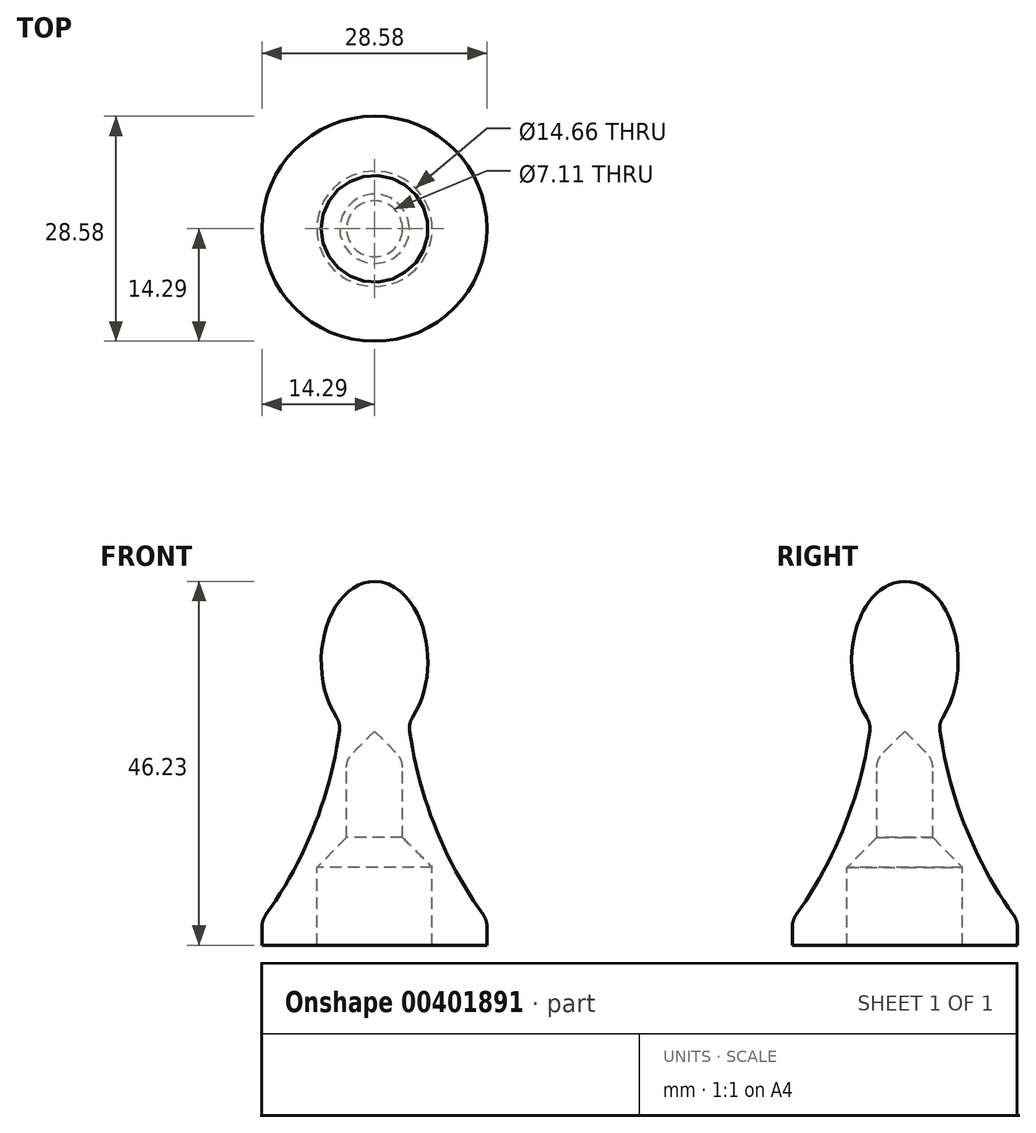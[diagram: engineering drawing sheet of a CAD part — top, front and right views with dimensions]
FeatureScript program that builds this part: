
annotation { "Feature Type Name" : "Feature", "Feature Type Description" : "" }
export const myFeature = defineFeature(function(context is Context, id is Id, definition is map)
    precondition{}
    {
        {
            var Q0;
            Q0=qCreatedBy(makeId("Front.planeOp"),FACE);
            var sketch = newSketch(context, id + "F0", { "sketchPlane" : qUnion([Q0])});
            skArc(sketch, "E0", {"start": v(-14.29, 3.18) * mm, "mid": v(-7.69, 15.07) * mm, "end": v(-4.32, 28.24) * mm});
            skLineSegment(sketch, "E1", {"start": v(-14.29, 3.17) * mm, "end": v(-14.29, 0) * mm});
            skLineSegment(sketch, "E2", {"start": v(-14.29, 0) * mm, "end": v(-7.33, 0) * mm});
            skLineSegment(sketch, "E3", {"start": v(0, 46.23) * mm, "end": v(0, 27.18) * mm});
            skLineSegment(sketch, "E4", {"start": v(-4.32, 28.24) * mm, "end": v(-1.02, 55.08) * mm, "construction": true});
            skEllipticalArc(sketch, "E5", {});
            skLineSegment(sketch, "E6", {"start": v(0, 27.18) * mm, "end": v(-2.81, 24.37) * mm});
            skLineSegment(sketch, "E7", {"start": v(-3.56, 22.57) * mm, "end": v(-3.56, 13.68) * mm});
            skLineSegment(sketch, "E8", {"start": v(-3.56, 13.68) * mm, "end": v(-7.33, 9.9) * mm});
            skLineSegment(sketch, "E9", {"start": v(-7.33, 9.9) * mm, "end": v(-7.33, 0) * mm});
            skLineSegment(sketch, "E10", {"start": v(0, 27.18) * mm, "end": v(0, 0) * mm, "construction": true});
            skLineSegment(sketch, "E11", {"start": v(-7.33, 0) * mm, "end": v(0, 0) * mm, "construction": true});
            skPoint(sketch, "E12.visualSharp", {"position": v(-3.56, 23.62) * mm});
            skArc(sketch, "E12.filletArc", {"start": v(-2.81, 24.37) * mm, "mid": v(-3.36, 23.54) * mm, "end": v(-3.56, 22.57) * mm});
            const initialGuessF0  = {"E5": [0, 0.036068, 0, 1, 0.01016, 0.006769100000000001, 0, 2.4498260338107896]};
            skSetInitialGuess(sketch, initialGuessF0);
            skSolve(sketch);
        }
        {
            var Q0;
            Q0 = qSketchRegion(id + "F0", true);
            var Q1;
            Q1=sQuery(id+"F0.wireOp",EDGE,"E3");
            revolve(context, id + "F1", {"entities" : qUnion([Q0]), "axis" : qUnion([Q1]), "revolveType" : RevolveType.FULL});
        }
        {
            var Q0;
            Q0=makeQuery(id+"F1.opRevolve","SWEPT_EDGE",EDGE,{"disambiguationData":[OSD([sQuery(id+"F0.wireOp",EDGE,"cC3xXklb-JENr-gKqO-IT1w-Tpzx20G1Xz3S"),sQuery(id+"F0.wireOp",EDGE,"E0")])]});
            fillet(context, id + "F2", {"entities" : qUnion([Q0]), "radius" : 2.54 * mm, "tangentPropagation" : true, "allowEdgeOverflow" : false});
        }
    });
